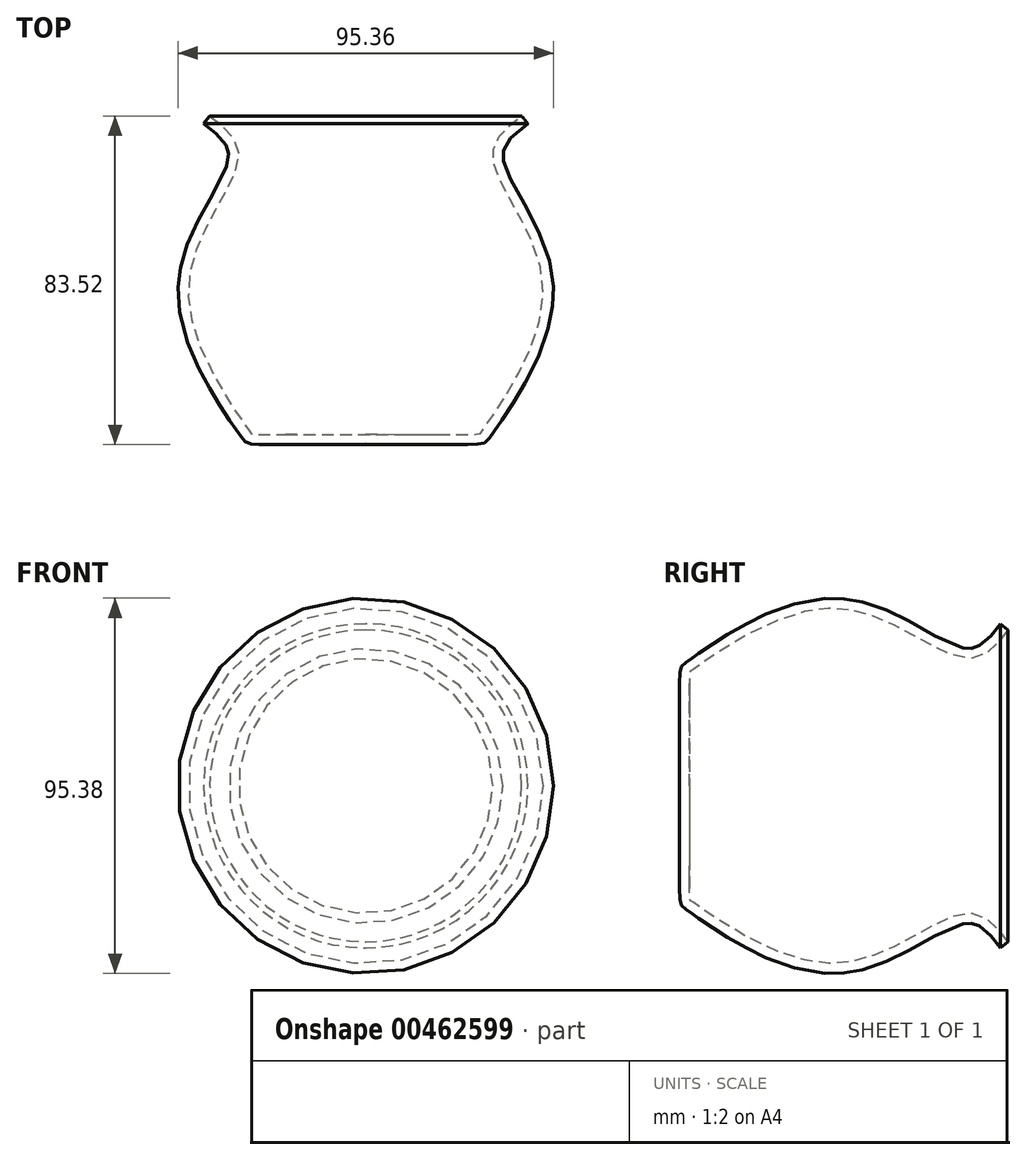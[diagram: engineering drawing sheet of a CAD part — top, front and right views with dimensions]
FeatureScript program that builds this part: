
annotation { "Feature Type Name" : "Feature", "Feature Type Description" : "" }
export const myFeature = defineFeature(function(context is Context, id is Id, definition is map)
    precondition{}
    {
        {
            var Q0;
            Q0=qCreatedBy(makeId("Top.planeOp"),FACE);
            var sketch = newSketch(context, id + "F0", { "sketchPlane" : qUnion([Q0])});
            skLineSegment(sketch, "E0", {"start": v(0, 51.05) * mm, "end": v(0, -62.33) * mm});
            skFitSpline(sketch, "E1", {"points": [v(-4.57, -35.2) * mm, v(28.96, -35.2) * mm, v(29.26, -34.9) * mm, v(45.11, 0) * mm, v(32.3, 35.2) * mm, v(41.76, 47.1) * mm], "startDerivative": vector(187.6, -2) * mm, "endDerivative": vector(84.44, 59.09) * mm});
            skFitSpline(sketch, "E2.0", {"points": [v(-4.6, -37.74) * mm, v(-2.64, -37.77) * mm, v(1.26, -37.8) * mm, v(6.97, -37.86) * mm, v(12.36, -37.9) * mm, v(16.47, -37.93) * mm, v(19.43, -37.94) * mm, v(21.48, -37.94) * mm, v(23.34, -37.93) * mm, v(24.7, -37.92) * mm, v(25.69, -37.9) * mm, v(26.36, -37.9) * mm, v(26.98, -37.88) * mm, v(27.53, -37.86) * mm, v(28.02, -37.84) * mm, v(28.38, -37.82) * mm, v(28.65, -37.8) * mm, v(28.83, -37.78) * mm, v(29.02, -37.76) * mm, v(29.2, -37.74) * mm, v(29.4, -37.7) * mm, v(29.63, -37.66) * mm, v(29.96, -37.56) * mm, v(30.3, -37.4) * mm, v(30.57, -37.22) * mm, v(30.82, -37.02) * mm, v(31.02, -36.81) * mm, v(31.17, -36.63) * mm, v(31.3, -36.44) * mm, v(31.38, -36.3) * mm, v(31.4, -36.26) * mm, v(31.42, -36.24) * mm, v(31.43, -36.23) * mm, v(31.46, -36.18) * mm, v(31.52, -36.09) * mm, v(31.63, -35.93) * mm, v(31.8, -35.67) * mm, v(32.09, -35.27) * mm, v(32.42, -34.8) * mm, v(32.8, -34.27) * mm, v(33.24, -33.66) * mm, v(33.86, -32.77) * mm, v(34.74, -31.5) * mm, v(35.9, -29.78) * mm, v(37.14, -27.85) * mm, v(38.44, -25.75) * mm, v(39.76, -23.5) * mm, v(41.51, -20.3) * mm, v(43.62, -16.03) * mm, v(45.4, -11.49) * mm, v(46.5, -7.76) * mm, v(47.15, -4.92) * mm, v(47.5, -2.55) * mm, v(47.64, -0.65) * mm, v(47.69, 1.25) * mm, v(47.57, 3.57) * mm, v(47.05, 7.18) * mm, v(45.87, 11.48) * mm, v(43.9, 16.27) * mm, v(41.65, 20.71) * mm, v(39.37, 24.8) * mm, v(37.3, 28.48) * mm, v(35.98, 31.2) * mm, v(35.28, 33.07) * mm, v(35, 34.1) * mm, v(34.88, 34.84) * mm, v(34.84, 35.33) * mm, v(34.84, 35.79) * mm, v(34.9, 36.37) * mm, v(35.05, 37.07) * mm, v(35.4, 37.9) * mm, v(35.9, 38.75) * mm, v(36.8, 39.91) * mm, v(38.3, 41.4) * mm, v(40.6, 43.19) * mm, v(42.33, 44.4) * mm, v(43.21, 45.01) * mm]});
            skLineSegment(sketch, "E3", {"start": v(39.62, 45.58) * mm, "end": v(41.2, 43.59) * mm});
            skSolve(sketch);
        }
        {
            var Q0;
            Q0 = qSketchRegion(id + "F0", true);
            var Q1;
            Q1=sQuery(id+"F0.wireOp",EDGE,"E0");
            revolve(context, id + "F1", {"entities" : qUnion([Q0]), "axis" : qUnion([Q1]), "revolveType" : RevolveType.FULL});
        }
    });
